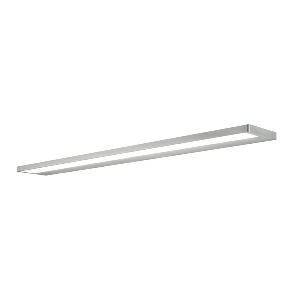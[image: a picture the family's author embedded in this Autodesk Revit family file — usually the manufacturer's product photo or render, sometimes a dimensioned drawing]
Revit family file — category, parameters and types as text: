
# Revit family: zera_wall_-_zew_7000_vtl_d_00812458_9f20
name_source: partatom
category: Lighting Fixtures
units: mm (PartAtom-declared; Revit-internal decimal feet)

## family parameters
Cut with Voids When Loaded = No
Host = Face
Light Source = No
Part Type = Normal
Room Calculation Point = No
Round Connector Dimension = Use Diameter
Shared = No

## types (1)
- ZERA.wall - ZEW 7000/VTL/D (1 x LED VTL, 6600 lm, 3000-6500K)
    Apparent Load = 50 VA
    Approval mark = CE
    CIE Flux Codes = 46 78 95 41 100
    Color Rendering = 80-89
    Color Temperature = 3000-6500K
    Control Gear = Electronic ballast
    Default Elevation = 2000 mm  [stored 6.56168 ft]
    Description = ZEW 7000/VTL|Wall-mounted luminaire|light source:      |work equipment: Electronic ballast dimable digital|luminous flux: 6600 lm|light distribution: Direct/indirect|class of protection: I|technology: Continuously dimmable|mains lead: Connector 5 pin|glare control: Diffusor|special features: Asymmetric radiation, Biodynamic light VTL, DALI Load 2x, DIN EN 60598-2-25, External control device required for DALI Device Type 6, Suitable as emergency lighting|
    Frequency = 50 Hz, 60 Hz
    Height = 29 mm
    Lamp = 1 x LED VTL
    Lamp Light Flux = 6600 lm
    Lamp count = 1
    Length = 1050 mm
    Luminous efficacy = 132 lm/W
    Manufacturer = Waldmann
    ModVariant = No
    Model = 00812458
    Mounting Place = Wall
    Mounting Type = Surface mounted
    Number of Poles = 1
    OnlyDefault = Yes
    Power Factor = 1
    Product Name = ZERA.wall - ZEW 7000/VTL/D
    Product group = Wall mounted Luminaire
    ProductGroupID = 20
    Protection Class = Protection class I
    Protection Degree = IP 20
    RLX_Detail_Level = 1
    RLX_Emergency_Light_Flux = 0 lm
    RLX_Emergency_Type = 0
    RLX_Emergency_Type_DB = No
    RlxData = <blob elided: 33645 chars, md5=e25f154e>
    Socket = socket
    Standby Power = 0 W
    System Light Flux = 6600 lm
    System Power = 50 W
    Type Comments = Product without accessories
    Type Image = zera_40_w.jpg
    URL = http://relux.com
    VarID = ---
    Voltage = 230 V
    Voltage Range = 220-240 V
    Weight = 0.00 kg
    Width = 142 mm

note: [stored X ft] marks values corroborated as IEEE doubles in the binary element streams (Revit-internal decimal feet)

## geometry (parser evidence)
native form markers: Blend x4, Sweep x15
no freeform markers — native parametric forms only
